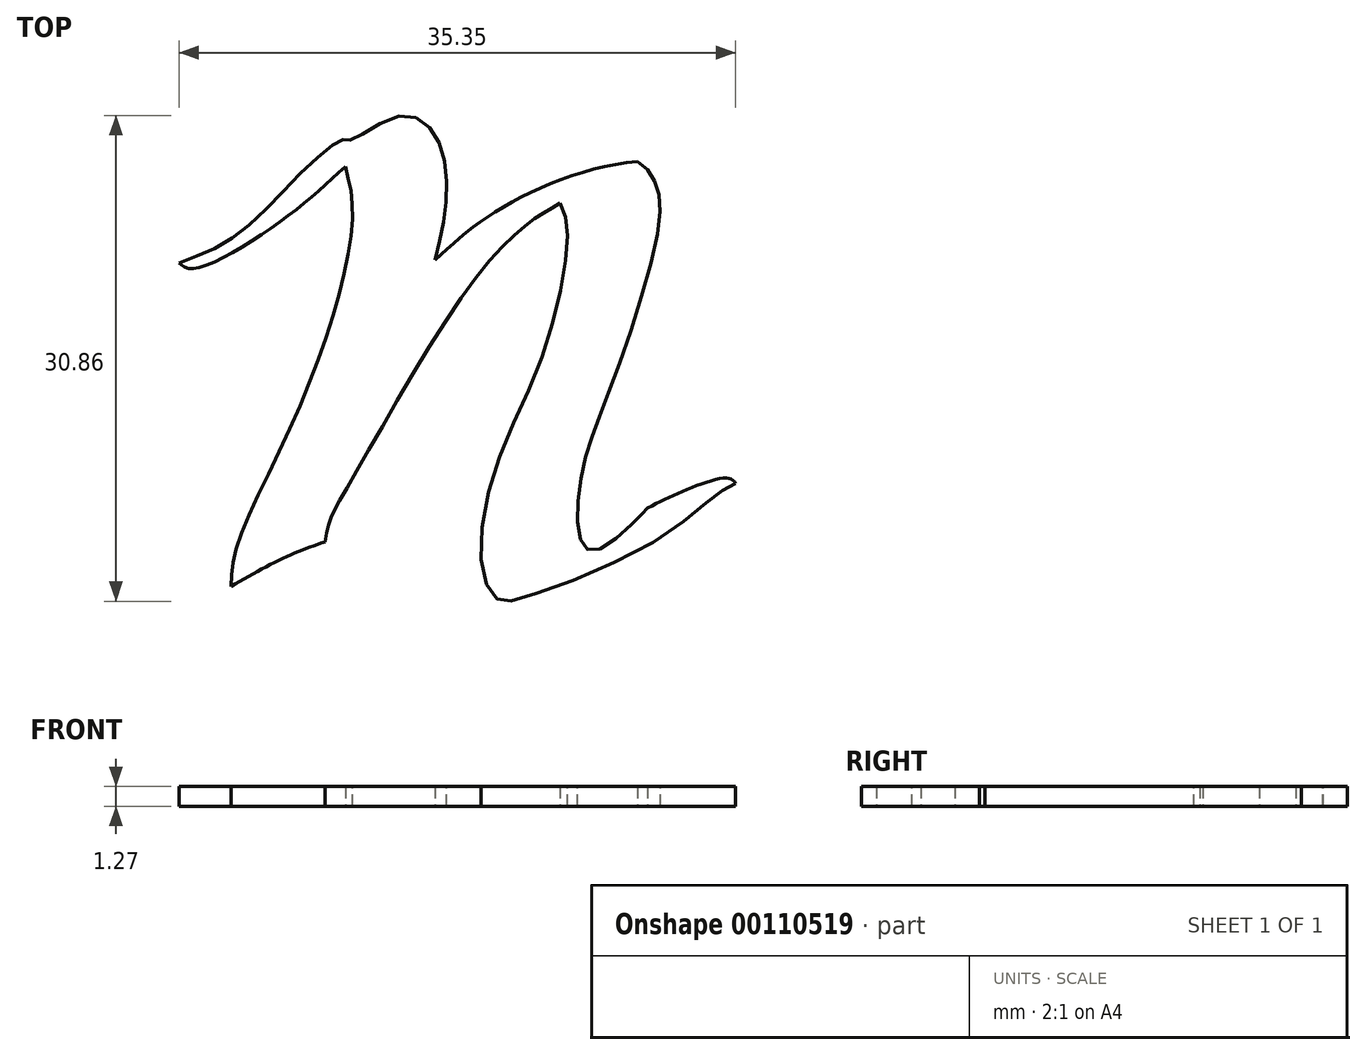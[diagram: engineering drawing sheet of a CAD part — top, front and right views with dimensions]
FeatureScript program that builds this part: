
annotation { "Feature Type Name" : "Feature", "Feature Type Description" : "" }
export const myFeature = defineFeature(function(context is Context, id is Id, definition is map)
    precondition{}
    {
        {
            var Q0;
            Q0=qCreatedBy(makeId("Top.planeOp"),FACE);
            var sketch = newSketch(context, id + "F0", { "sketchPlane" : qUnion([Q0])});
            skFitSpline(sketch, "E0", {"points": [v(-52.45, 6.15) * mm, v(-48.9, 7.84) * mm, v(-44.8, 11.75) * mm, v(-42.05, 13.97) * mm, v(-41.52, 13.97) * mm, v(-38.4, 15.48) * mm, v(-36.1, 14.15) * mm, v(-35.47, 10.24) * mm, v(-36.19, 6.33) * mm], "startDerivative": vector(26.24, 9.5) * mm, "endDerivative": vector(-6.7, -27.61) * mm});
            skFitSpline(sketch, "E1", {"points": [v(-36.19, 6.33) * mm, v(-31.74, 9.77) * mm, v(-23.32, 12.58) * mm], "startDerivative": vector(8.9, 8.37) * mm, "endDerivative": vector(15.9, 1.3) * mm});
            skFitSpline(sketch, "E2", {"points": [v(-23.32, 12.58) * mm, v(-22.22, 11.3) * mm, v(-21.97, 8.49) * mm, v(-25.05, -1.83) * mm, v(-26.75, -6.74) * mm, v(-27.02, -11.14) * mm, v(-26.08, -12.14) * mm, v(-23.32, -10.08) * mm, v(-22.68, -9.4) * mm], "startDerivative": vector(16.58, -7.8) * mm, "endDerivative": vector(6.94, 7.49) * mm});
            skFitSpline(sketch, "E3", {"points": [v(-22.68, -9.4) * mm, v(-19.88, -8.12) * mm, v(-17.53, -7.53) * mm, v(-17.1, -7.85) * mm], "startDerivative": vector(6.2, 3.05) * mm, "endDerivative": vector(1.78, -2.27) * mm});
            skFitSpline(sketch, "E4", {"points": [v(-17.1, -7.85) * mm, v(-18.25, -8.52) * mm, v(-22.23, -11.55) * mm, v(-30.63, -15.13) * mm, v(-32.22, -15.2) * mm, v(-33.18, -13.3) * mm, v(-32.42, -7.13) * mm, v(-29.63, -0.48) * mm, v(-27.98, 5.61) * mm, v(-27.82, 8.74) * mm, v(-28.24, 9.94) * mm], "startDerivative": vector(-18.14, -8.86) * mm, "endDerivative": vector(-8.69, 18.7) * mm});
            skFitSpline(sketch, "E5", {"points": [v(-28.24, 9.94) * mm, v(-29.92, 8.9) * mm, v(-34.1, 4.53) * mm, v(-41.82, -8.24) * mm, v(-42.86, -10.18) * mm, v(-43.18, -11.56) * mm], "startDerivative": vector(-11.79, -6.5) * mm, "endDerivative": vector(-2.24, -12.64) * mm});
            skFitSpline(sketch, "E6", {"points": [v(-43.18, -11.56) * mm, v(-45.72, -12.56) * mm, v(-49.15, -14.4) * mm], "startDerivative": vector(-5.4, -1.93) * mm, "endDerivative": vector(-6.5, -3.67) * mm});
            skFitSpline(sketch, "E7", {"points": [v(-49.15, -14.4) * mm, v(-48.74, -11.75) * mm, v(-45.45, -4.5) * mm, v(-42.27, 4.19) * mm, v(-41.42, 9.63) * mm, v(-41.88, 12.26) * mm], "startDerivative": vector(0.79, 16.57) * mm, "endDerivative": vector(-4.48, 16.98) * mm});
            skFitSpline(sketch, "E8", {"points": [v(-41.88, 12.26) * mm, v(-46.35, 8.53) * mm, v(-51.6, 5.78) * mm, v(-52.45, 6.15) * mm], "startDerivative": vector(-9.57, -8.79) * mm, "endDerivative": vector(-3.92, 3.49) * mm});
            skSolve(sketch);
        }
        {
            var Q0;
            Q0 = qSketchRegion(id + "F0", true);
            extrude(context, id + "F1", {"entities" : qUnion([Q0]), "depth" : 1.27 * mm});
        }
    });
